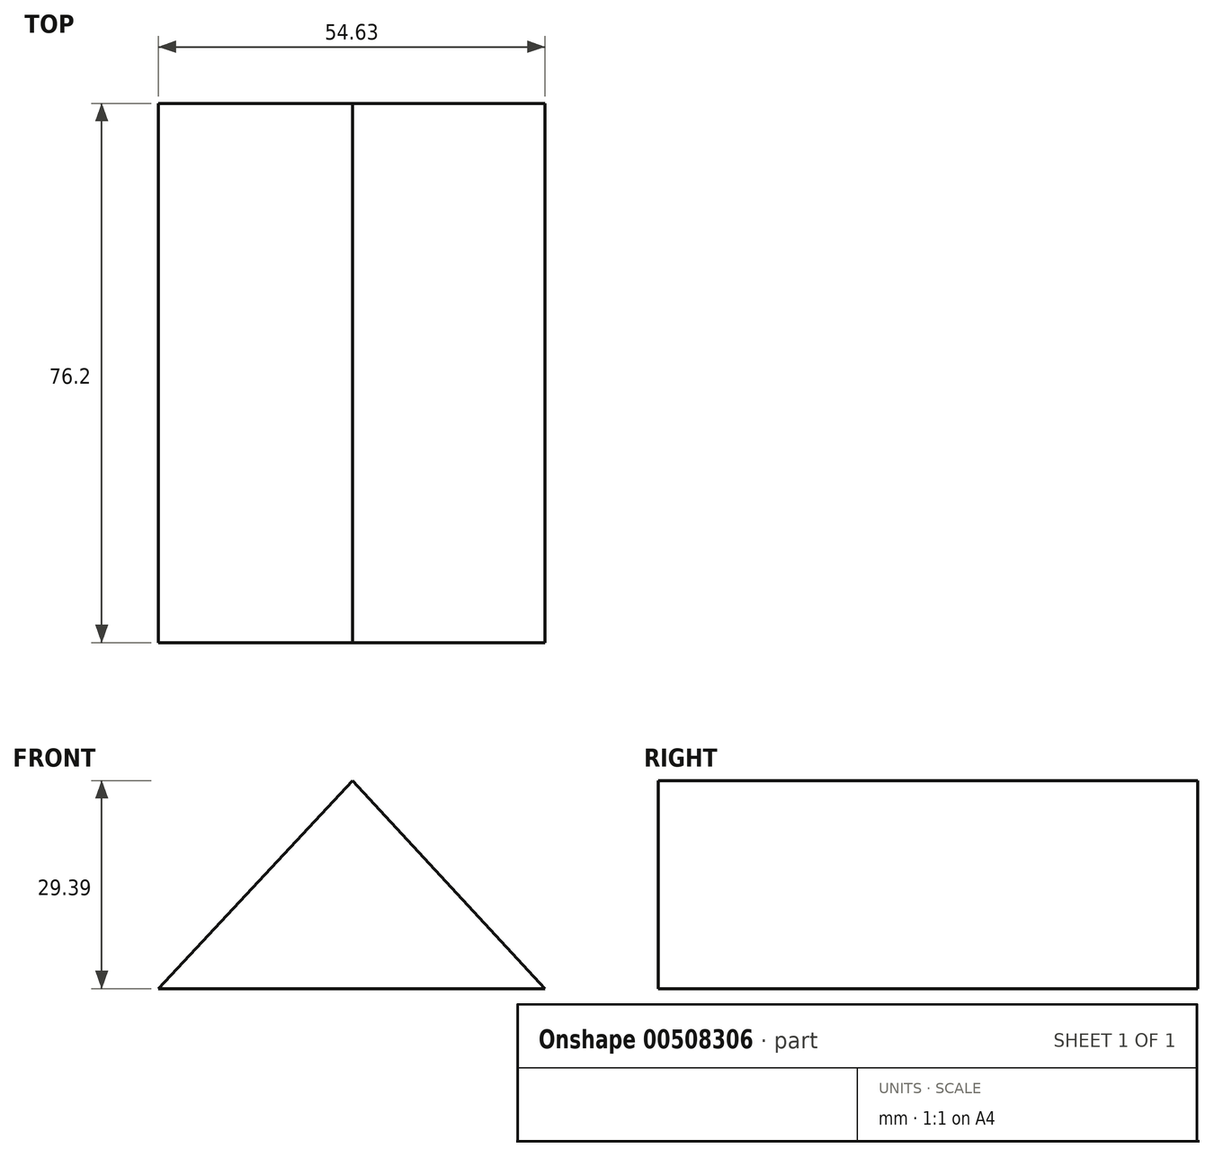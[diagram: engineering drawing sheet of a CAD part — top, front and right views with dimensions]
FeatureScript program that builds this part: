
annotation { "Feature Type Name" : "Feature", "Feature Type Description" : "" }
export const myFeature = defineFeature(function(context is Context, id is Id, definition is map)
    precondition{}
    {
        {
            var Q0;
            Q0=qCreatedBy(makeId("Front.planeOp"),FACE);
            var sketch = newSketch(context, id + "F0", { "sketchPlane" : qUnion([Q0])});
            skLineSegment(sketch, "E0", {"start": v(-27.42, 0) * mm, "end": v(27.2, 0) * mm});
            skLineSegment(sketch, "E1", {"start": v(-27.42, 0) * mm, "end": v(0, 29.4) * mm});
            skLineSegment(sketch, "E2", {"start": v(0, 29.4) * mm, "end": v(27.2, 0) * mm});
            skLineSegment(sketch, "E3", {"start": v(0, 29.39) * mm, "end": v(0, 0) * mm});
            skSolve(sketch);
        }
        {
            var Q0;
            Q0 = qSketchRegion(id + "F0", true);
            extrude(context, id + "F1", {"entities" : qUnion([Q0]), "depth" : 76.2 * mm});
        }
    });
